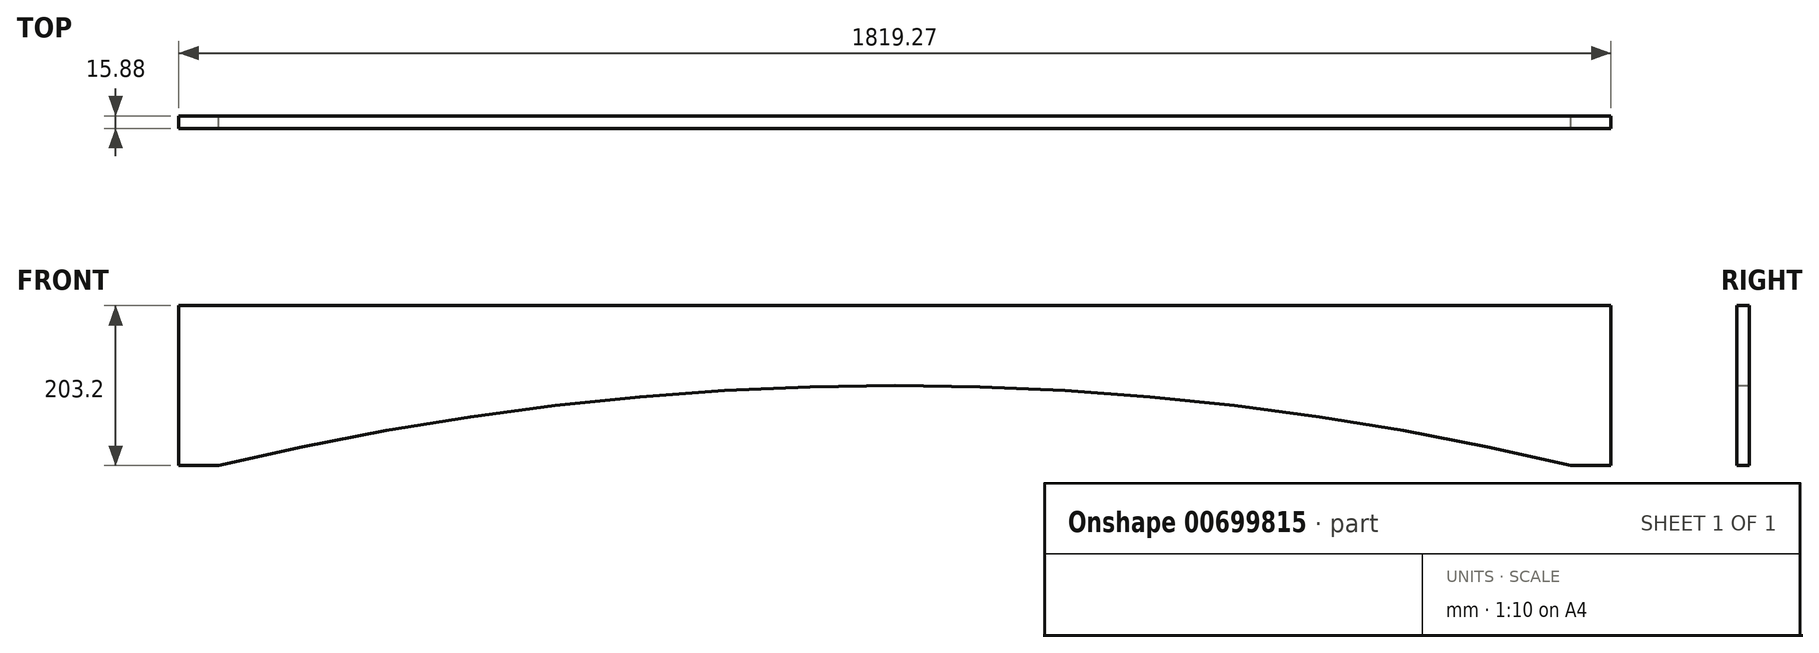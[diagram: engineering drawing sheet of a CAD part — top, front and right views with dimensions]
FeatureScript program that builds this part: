
annotation { "Feature Type Name" : "Feature", "Feature Type Description" : "" }
export const myFeature = defineFeature(function(context is Context, id is Id, definition is map)
    precondition{}
    {
        {
            var Q0;
            Q0=qCreatedBy(makeId("Front.planeOp"),FACE);
            var sketch = newSketch(context, id + "F0", { "sketchPlane" : qUnion([Q0])});
            skLineSegment(sketch, "E0", {"start": v(-959.5, 64.66) * mm, "end": v(859.77, 64.66) * mm});
            skLineSegment(sketch, "E1", {"start": v(859.77, 64.66) * mm, "end": v(859.77, -138.54) * mm});
            skLineSegment(sketch, "E2", {"start": v(-959.5, 64.66) * mm, "end": v(-959.5, -138.54) * mm});
            skLineSegment(sketch, "E3", {"start": v(-959.5, -138.54) * mm, "end": v(-908.7, -138.54) * mm});
            skLineSegment(sketch, "E4", {"start": v(859.77, -138.54) * mm, "end": v(808.97, -138.54) * mm});
            skArc(sketch, "E5", {"start": v(808.97, -138.54) * mm, "mid": v(-49.86, -36.94) * mm, "end": v(-908.7, -138.54) * mm});
            skPoint(sketch, "E6.start.orphan", {"position": v(-49.86, -138.54) * mm});
            skSolve(sketch);
        }
        {
            var Q0;
            Q0 = qSketchRegion(id + "F0", true);
            extrude(context, id + "F1", {"entities" : qUnion([Q0]), "depth" : 15.88 * mm, "offsetDistance" : 25.4 * mm});
        }
    });
